# Revit family: Sanitary_Accessories_AXOR_42830XXX-AXOR-Universal-Softsquare-Rail_new
name_source: partatom
category: Furniture
revit_build: Autodesk Revit 2018 (Build: 20170223_1515(x64)
units: mm (PartAtom-declared; Revit-internal decimal feet)

## family parameters
Always vertical = No
Cut with Voids When Loaded = No
OmniClass Number = 23.31.25.25
OmniClass Title = Towel Bars
Room Calculation Point = No
Shared = No
Work Plane-Based = Yes

## types (1)
- Default - please load Revit Family Type Catalog
    Always visible = Yes
    BIMobject category = Accessories
    Default Elevation = 1219.2 mm  [stored 4 ft]
    Description = AXOR Universal Softsquare Rail grab bar 300 mm
    Design country = Germany
    EAN code = 4059625428511
    Edition number = 1
    GTIN code = https://4059625428511
    IFC Classification = Furnishing Element
    Manufacturer = AXOR
    Manufacturer country = Germany
    Manufacturer name = AXOR
    Material 1 = AXOR - Metal - 000 Chrome
    Material main = Metal
    Material secondary = Chrome
    Model = 42830XXX
    OmniClass Code = 23-31 25 25
    OmniClass Description = Towel Bars
    Product Guid = b97c6469-50d4-49d2-ad91-d72f1d4c1627
    Product SKU = 42830XXX
    Product data url = https://bimobject.com
    Product family = AXOR Universal Softsquare
    Product group = Grab bars
    Product name = 42830XXX AXOR Universal Softsquare Rail grab bar 300 mm
    QR code = https://bimobject.com
    URL = https://www.axor-design.com
    Weight Net (Kg) = 1.5

note: [stored X ft] marks values corroborated as IEEE doubles in the binary element streams (Revit-internal decimal feet)

## geometry (parser evidence)
native form markers: Sweep x3
no freeform markers — native parametric forms only
